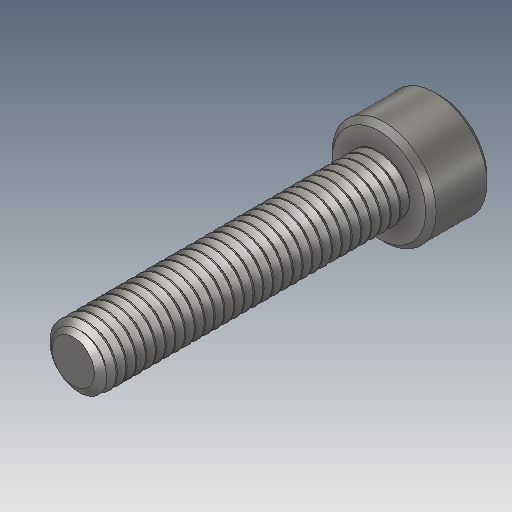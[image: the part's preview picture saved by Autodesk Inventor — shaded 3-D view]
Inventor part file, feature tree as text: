
AUTODESK INVENTOR PART (.ipt)
format: ipt  version: 2017 (Build 210142000, 142)  size: 908,800 bytes
history: native  units: in
note: dims shown in document units (in); Inventor stores cm internally (conversion verified against a paired STEP export)
features: chamfer x1
ambient origin geometry x8: Origin, YZ Plane, XZ Plane, XY Plane, X Axis, Y Axis, Z Axis, Center Point
bodies: Solid1 (feature_tree)
feature tree (1):
  chamfer  "Chamfer1"  [1 undecoded]
note: 1 required parameter value undecoded (feature->parameter linkage not recoverable at this tier; creation-order binding heuristic only, values carry confidence <= 0.55)
